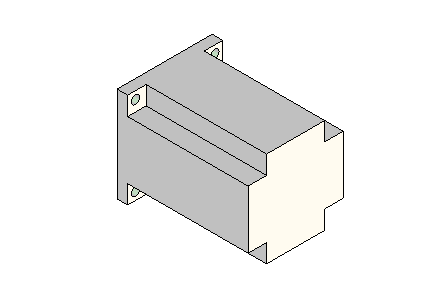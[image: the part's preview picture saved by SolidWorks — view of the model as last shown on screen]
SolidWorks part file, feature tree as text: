
SOLIDWORKS PART (.sldprt)
format: sldprt  version: not decoded by parser v0  size: 226,304 bytes
history: native  units: mm
features: sketch x5, extrude x3, cut_extrude x2 (+11 scaffold rows collapsed)
feature tree (21):
  scaffold x11  (default folders/planes/origin — collapsed)
  sketch  "Sketch1"  dims[D1=57.15mm D2=57.15mm]
  extrude  "Extrude1"  Depth=78.74mm
  sketch  "Sketch2"  dims[D1=38.1mm]
  extrude  "Extrude2"  Depth=1.524mm
  sketch  "Sketch3"  dims[D1=6.35mm]
  extrude  "Extrude3"  Depth=20.574mm
  sketch  "Sketch4"  dims[D1=11.1125mm]
  cut_extrude  "Cut-Extrude1"  Depth=6.35mm
  sketch  "Sketch5"  dims[c1.D1=5.08mm c1.D2=5.08mm c1.D3=5.08mm c1.D4=5.08mm c1.D5=5.08mm c1.D6=5.08mm c1.D7=5.08mm c1.D8=5.08mm c1.D9=5.08mm c2.D2=47.752mm c2.D3=47.752mm c2.D4=47.752mm c2.D5=47.752mm c2.D6=23.876mm c2.D7=23.876mm c2.D8=23.876mm c2.D9=23.876mm]
  cut_extrude  "Cut-Extrude2"  [1 undecoded]
decode coverage: 9 of 10 modeling features carry decoded parameters
note: 1 parameter value undecoded
note: suppression state not decoded; provenance and decode notes live in map.json
